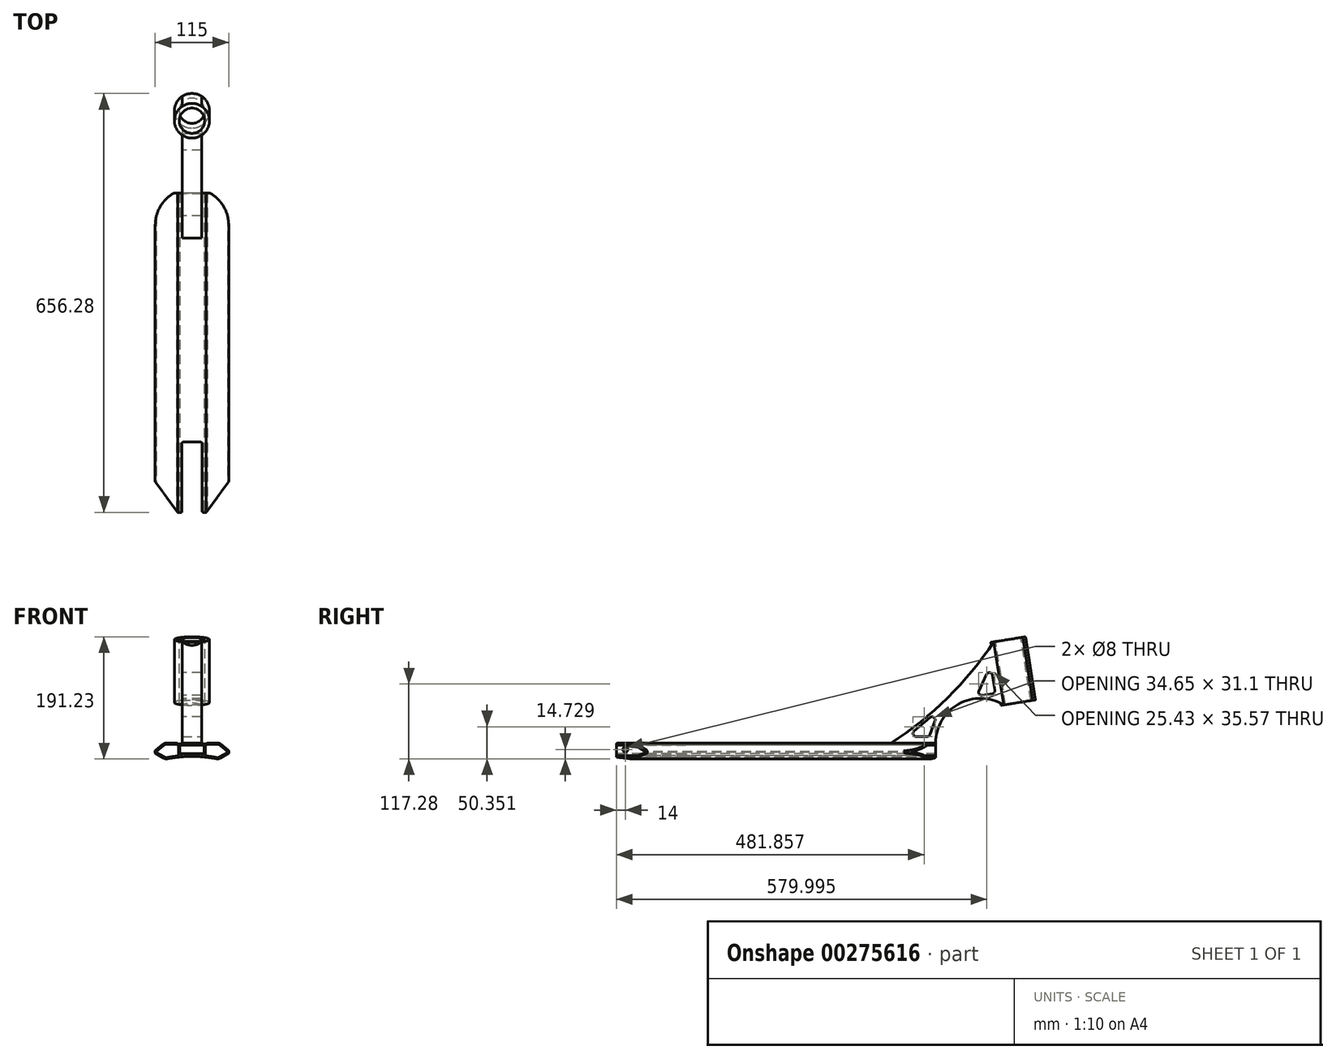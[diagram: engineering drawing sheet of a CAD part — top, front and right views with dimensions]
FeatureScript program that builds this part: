
annotation { "Feature Type Name" : "Feature", "Feature Type Description" : "" }
export const myFeature = defineFeature(function(context is Context, id is Id, definition is map)
    precondition{}
    {
        {
            var Q0;
            Q0=qCreatedBy(makeId("Front.planeOp"),FACE);
            var sketch = newSketch(context, id + "F0", { "sketchPlane" : qUnion([Q0])});
            skLineSegment(sketch, "E0", {"start": v(0, 45.15) * mm, "end": v(0, 0) * mm, "construction": true});
            skLineSegment(sketch, "E1", {"start": v(0, 10.68) * mm, "end": v(22.5, 10.68) * mm});
            skLineSegment(sketch, "E2", {"start": v(22.5, 10.68) * mm, "end": v(22.5, 11.98) * mm});
            skLineSegment(sketch, "E3", {"start": v(22.5, 11.98) * mm, "end": v(43.22, 11.98) * mm});
            skLineSegment(sketch, "E4", {"start": v(43.22, 11.98) * mm, "end": v(57.5, 0) * mm});
            skLineSegment(sketch, "E5", {"start": v(57.5, 0) * mm, "end": v(57.5, -4) * mm});
            skLineSegment(sketch, "E6", {"start": v(57.5, -4) * mm, "end": v(41.36, -13.32) * mm});
            skLineSegment(sketch, "E7.MirrorCS", {"start": v(0, 10.68) * mm, "end": v(-22.5, 10.68) * mm});
            skLineSegment(sketch, "E8.MirrorCS", {"start": v(-22.5, 10.68) * mm, "end": v(-22.5, 11.98) * mm});
            skLineSegment(sketch, "E9.MirrorCS", {"start": v(-22.5, 11.98) * mm, "end": v(-43.22, 11.98) * mm});
            skLineSegment(sketch, "E10.MirrorCS", {"start": v(-43.22, 11.98) * mm, "end": v(-57.5, 0) * mm});
            skLineSegment(sketch, "E11.MirrorCS", {"start": v(-57.5, 0) * mm, "end": v(-57.5, -4) * mm});
            skLineSegment(sketch, "E12.MirrorCS", {"start": v(-57.5, -4) * mm, "end": v(-41.36, -13.32) * mm});
            skArc(sketch, "E13", {"start": v(41.36, -13.32) * mm, "mid": v(0, -9) * mm, "end": v(-41.36, -13.32) * mm});
            skSolve(sketch);
        }
        {
            var Q0;
            Q0=qSketchRegion(id+"F0",true);
            extrude(context, id + "F1", {"entities" : qUnion([Q0]), "endBound" : BoundingType.SYMMETRIC, "depth" : 500 * mm});
        }
        {
            var Q0;
            Q0=makeQuery(id+"F1.opExtrude","CAP_FACE",FACE,{"disambiguationData":[OSD([sQuery(id+"F0.wireOp",EDGE,"E1"),sQuery(id+"F0.wireOp",EDGE,"E2"),sQuery(id+"F0.wireOp",EDGE,"E3"),sQuery(id+"F0.wireOp",EDGE,"E4"),sQuery(id+"F0.wireOp",EDGE,"E5"),sQuery(id+"F0.wireOp",EDGE,"E6"),sQuery(id+"F0.wireOp",EDGE,"E7.MirrorCS"),sQuery(id+"F0.wireOp",EDGE,"E8.MirrorCS"),sQuery(id+"F0.wireOp",EDGE,"E9.MirrorCS"),sQuery(id+"F0.wireOp",EDGE,"E10.MirrorCS"),sQuery(id+"F0.wireOp",EDGE,"E11.MirrorCS"),sQuery(id+"F0.wireOp",EDGE,"E12.MirrorCS"),sQuery(id+"F0.wireOp",EDGE,"E13")])],"isStart":false});
            var sketch = newSketch(context, id + "F2", { "sketchPlane" : qUnion([Q0])});
            skPoint(sketch, "E14.firstSnap0", {"position": v(-50.36, 8.68) * mm});
            skLineSegment(sketch, "E14.top", {"start": v(-19, -4.32) * mm, "end": v(19, -4.32) * mm});
            skLineSegment(sketch, "E14.left", {"start": v(-19, 8.68) * mm, "end": v(-19, -4.32) * mm});
            skLineSegment(sketch, "E14.right", {"start": v(19, 8.68) * mm, "end": v(19, -4.32) * mm});
            skLineSegment(sketch, "E15", {"start": v(-19, 8.68) * mm, "end": v(19, 8.68) * mm});
            skSolve(sketch);
        }
        {
            var Q0;
            Q0=qSketchRegion(id+"F2",true);
            extrude(context, id + "F3", {"entities" : qUnion([Q0]), "operationType" : NewBodyOperationType.REMOVE, "endBound" : BoundingType.THROUGH_ALL, "oppositeDirection" : true, "depth" : 500 * mm});
        }
        {
            var Q0;
            Q0=makeQuery(id+"F1.opExtrude","SWEPT_EDGE",EDGE,{"disambiguationData":[OSD([sQuery(id+"F0.wireOp",EDGE,"E8.MirrorCS"),sQuery(id+"F0.wireOp",EDGE,"E9.MirrorCS")])]});
            var Q1;
            Q1=makeQuery(id+"F1.opExtrude","SWEPT_EDGE",EDGE,{"disambiguationData":[OSD([sQuery(id+"F0.wireOp",EDGE,"E2"),sQuery(id+"F0.wireOp",EDGE,"E3")])]});
            fillet(context, id + "F4", {"entities" : qUnion([Q0, Q1]), "radius" : 2 * mm, "tangentPropagation" : true, "allowEdgeOverflow" : false});
        }
        {
            var Q0;
            Q0=makeQuery(id+"F1.opExtrude","SWEPT_EDGE",EDGE,{"disambiguationData":[OSD([sQuery(id+"F0.wireOp",EDGE,"E12.MirrorCS"),sQuery(id+"F0.wireOp",EDGE,"E13")])]});
            var Q1;
            Q1=makeQuery(id+"F1.opExtrude","SWEPT_EDGE",EDGE,{"disambiguationData":[OSD([sQuery(id+"F0.wireOp",EDGE,"E6"),sQuery(id+"F0.wireOp",EDGE,"E13")])]});
            var Q2;
            Q2=makeQuery(id+"F1.opExtrude","SWEPT_EDGE",EDGE,{"disambiguationData":[OSD([sQuery(id+"F0.wireOp",EDGE,"E9.MirrorCS"),sQuery(id+"F0.wireOp",EDGE,"E10.MirrorCS")])]});
            var Q3;
            Q3=makeQuery(id+"F1.opExtrude","SWEPT_EDGE",EDGE,{"disambiguationData":[OSD([sQuery(id+"F0.wireOp",EDGE,"E3"),sQuery(id+"F0.wireOp",EDGE,"E4")])]});
            fillet(context, id + "F5", {"entities" : qUnion([Q0, Q1, Q2, Q3]), "radius" : 9 * mm, "tangentPropagation" : true, "allowEdgeOverflow" : false});
        }
        {
            var Q0;
            Q0=makeQuery(id+"F1.opExtrude","SWEPT_EDGE",EDGE,{"disambiguationData":[OSD([sQuery(id+"F0.wireOp",EDGE,"E4"),sQuery(id+"F0.wireOp",EDGE,"E5")])]});
            var Q1;
            Q1=makeQuery(id+"F1.opExtrude","SWEPT_EDGE",EDGE,{"disambiguationData":[OSD([sQuery(id+"F0.wireOp",EDGE,"E5"),sQuery(id+"F0.wireOp",EDGE,"E6")])]});
            var Q2;
            Q2=makeQuery(id+"F1.opExtrude","SWEPT_EDGE",EDGE,{"disambiguationData":[OSD([sQuery(id+"F0.wireOp",EDGE,"E10.MirrorCS"),sQuery(id+"F0.wireOp",EDGE,"E11.MirrorCS")])]});
            var Q3;
            Q3=makeQuery(id+"F1.opExtrude","SWEPT_EDGE",EDGE,{"disambiguationData":[OSD([sQuery(id+"F0.wireOp",EDGE,"E11.MirrorCS"),sQuery(id+"F0.wireOp",EDGE,"E12.MirrorCS")])]});
            fillet(context, id + "F6", {"entities" : qUnion([Q0, Q1, Q2, Q3]), "radius" : 1 * mm, "tangentPropagation" : true, "allowEdgeOverflow" : false});
        }
        {
            var Q0;
            Q0=makeQuery(id+"F1.opExtrude","CAP_FACE",FACE,{"disambiguationData":[OSD([sQuery(id+"F0.wireOp",EDGE,"E1"),sQuery(id+"F0.wireOp",EDGE,"E2"),sQuery(id+"F0.wireOp",EDGE,"E3"),sQuery(id+"F0.wireOp",EDGE,"E4"),sQuery(id+"F0.wireOp",EDGE,"E5"),sQuery(id+"F0.wireOp",EDGE,"E6"),sQuery(id+"F0.wireOp",EDGE,"E7.MirrorCS"),sQuery(id+"F0.wireOp",EDGE,"E8.MirrorCS"),sQuery(id+"F0.wireOp",EDGE,"E9.MirrorCS"),sQuery(id+"F0.wireOp",EDGE,"E10.MirrorCS"),sQuery(id+"F0.wireOp",EDGE,"E11.MirrorCS"),sQuery(id+"F0.wireOp",EDGE,"E12.MirrorCS"),sQuery(id+"F0.wireOp",EDGE,"E13")])],"isStart":false});
            var sketch = newSketch(context, id + "F7", { "sketchPlane" : qUnion([Q0])});
            skLineSegment(sketch, "E16.0", {"start": v(-22.5, 10.68) * mm, "end": v(-21, 10.68) * mm});
            skPoint(sketch, "E17.0", {"position": v(-23.23, 11.62) * mm});
            skLineSegment(sketch, "E18.0", {"start": v(-24.37, 11.98) * mm, "end": v(-39.95, 11.98) * mm});
            skArc(sketch, "E19.0", {"start": v(-39.95, 11.98) * mm, "mid": v(-43.02, 11.44) * mm, "end": v(-45.73, 9.88) * mm});
            skLineSegment(sketch, "E20.0", {"start": v(-45.73, 9.88) * mm, "end": v(-57.14, 0.3) * mm});
            skPoint(sketch, "E21.0", {"position": v(-57.4, -0.04) * mm});
            skPoint(sketch, "E22.0", {"position": v(-57.5, -1.94) * mm});
            skPoint(sketch, "E23.0", {"position": v(-57, -4.29) * mm});
            skLineSegment(sketch, "E24.0", {"start": v(-57, -4.29) * mm, "end": v(-44.3, -11.62) * mm});
            skArc(sketch, "E25.0", {"start": v(-44.3, -11.62) * mm, "mid": v(-41.3, -12.7) * mm, "end": v(-38.1, -12.66) * mm});
            skArc(sketch, "E26.0", {"start": v(-21, -10.1) * mm, "mid": v(-29.57, -11.2) * mm, "end": v(-38.1, -12.66) * mm});
            skLineSegment(sketch, "E27", {"start": v(-21, 8.68) * mm, "end": v(-21, -8.1) * mm});
            skLineSegment(sketch, "E28.0", {"start": v(-44.45, 8.34) * mm, "end": v(-55.86, -1.23) * mm});
            skArc(sketch, "E28.1", {"start": v(-39.95, 9.98) * mm, "mid": v(-42.34, 9.56) * mm, "end": v(-44.45, 8.34) * mm});
            skLineSegment(sketch, "E29.0", {"start": v(-24.37, 9.98) * mm, "end": v(-39.95, 9.98) * mm});
            skLineSegment(sketch, "E30.0", {"start": v(-22.5, 8.68) * mm, "end": v(-21, 8.68) * mm});
            skFitSpline(sketch, "E31", {"points": [v(-24.37, 9.98) * mm, v(-22.5, 8.68) * mm], "startDerivative": vector(1.87, -1.3) * mm, "endDerivative": vector(1.87, -1.3) * mm});
            skFitSpline(sketch, "E32", {"points": [v(-23.12, 9.11) * mm, v(-23.48, 9.36) * mm], "startDerivative": vector(-0.35, 0.24) * mm, "endDerivative": vector(-0.35, 0.24) * mm});
            skLineSegment(sketch, "E33.0", {"start": v(-56, -2.56) * mm, "end": v(-43.3, -9.88) * mm});
            skArc(sketch, "E33.1", {"start": v(-43.3, -9.88) * mm, "mid": v(-40.96, -10.73) * mm, "end": v(-38.47, -10.7) * mm});
            skArc(sketch, "E33.2", {"start": v(-21, -8.1) * mm, "mid": v(-29.77, -9.2) * mm, "end": v(-38.47, -10.7) * mm});
            skLineSegment(sketch, "E34", {"start": v(-55.86, -1.23) * mm, "end": v(-56, -2.56) * mm});
            skLineSegment(sketch, "E35.MirrorCS", {"start": v(21, 8.68) * mm, "end": v(21, -8.1) * mm});
            skArc(sketch, "E36.MirrorCS", {"start": v(21, -8.1) * mm, "mid": v(29.77, -9.2) * mm, "end": v(38.47, -10.7) * mm});
            skArc(sketch, "E37.MirrorCS", {"start": v(43.3, -9.88) * mm, "mid": v(40.96, -10.73) * mm, "end": v(38.47, -10.7) * mm});
            skLineSegment(sketch, "E38.MirrorCS", {"start": v(56, -2.56) * mm, "end": v(43.3, -9.88) * mm});
            skLineSegment(sketch, "E39.MirrorCS", {"start": v(55.86, -1.23) * mm, "end": v(56, -2.56) * mm});
            skLineSegment(sketch, "E40.MirrorCS", {"start": v(44.45, 8.34) * mm, "end": v(55.86, -1.23) * mm});
            skArc(sketch, "E41.MirrorCS", {"start": v(39.95, 9.98) * mm, "mid": v(42.34, 9.56) * mm, "end": v(44.45, 8.34) * mm});
            skLineSegment(sketch, "E42.MirrorCS", {"start": v(24.37, 9.98) * mm, "end": v(39.95, 9.98) * mm});
            skLineSegment(sketch, "E43.MirrorCS", {"start": v(22.5, 8.68) * mm, "end": v(21, 8.68) * mm});
            skLineSegment(sketch, "E44", {"start": v(24.37, 9.98) * mm, "end": v(22.5, 8.68) * mm});
            skSolve(sketch);
        }
        {
            var Q0;
            Q0=qSketchRegion(id+"F7",true);
            extrude(context, id + "F8", {"entities" : qUnion([Q0]), "operationType" : NewBodyOperationType.REMOVE, "endBound" : BoundingType.THROUGH_ALL, "oppositeDirection" : true, "depth" : 25 * mm});
        }
        {
            var Q0;
            Q0=qSketchRegion(id+"F7",true);
            extrude(context, id + "F9", {"entities" : qUnion([Q0]), "operationType" : NewBodyOperationType.REMOVE, "endBound" : BoundingType.THROUGH_ALL, "oppositeDirection" : true, "depth" : 25 * mm});
        }
        {
            var Q0;
            Q0=makeQuery(id+"F1.opExtrude","SWEPT_FACE",FACE,{"disambiguationData":[OSD([sQuery(id+"F0.wireOp",EDGE,"E1"),sQuery(id+"F0.wireOp",EDGE,"E7.MirrorCS")])]});
            var sketch = newSketch(context, id + "F10", { "sketchPlane" : qUnion([Q0])});
            skArc(sketch, "E45", {"start": v(57.5, 200) * mm, "mid": v(0, 257.5) * mm, "end": v(-57.5, 200) * mm});
            skLineSegment(sketch, "E46", {"start": v(-57.5, 280) * mm, "end": v(57.5, 280) * mm});
            skLineSegment(sketch, "E47", {"start": v(57.5, 200) * mm, "end": v(57.5, 280) * mm});
            skPoint(sketch, "E48.orphan", {"position": v(63.8, 280) * mm});
            skLineSegment(sketch, "E49", {"start": v(-57.5, 200) * mm, "end": v(-57.5, 280) * mm});
            skPoint(sketch, "E50.orphan", {"position": v(-57.5, 278.01) * mm});
            skSolve(sketch);
        }
        {
            var Q0;
            Q0=qSketchRegion(id+"F10",true);
            extrude(context, id + "F11", {"entities" : qUnion([Q0]), "operationType" : NewBodyOperationType.REMOVE, "endBound" : BoundingType.SYMMETRIC, "oppositeDirection" : true, "depth" : 100 * mm});
        }
        {
            var Q0;
            Q0=makeQuery(id+"F1.opExtrude","SWEPT_FACE",FACE,{"disambiguationData":[OSD([sQuery(id+"F0.wireOp",EDGE,"E9.MirrorCS")])]});
            var sketch = newSketch(context, id + "F12", { "sketchPlane" : qUnion([Q0])});
            skLineSegment(sketch, "E51", {"start": v(-68, -187.37) * mm, "end": v(-22.5, -250) * mm});
            skLineSegment(sketch, "E52", {"start": v(-22.5, -250) * mm, "end": v(-16, -250) * mm});
            skLineSegment(sketch, "E53", {"start": v(-16, -250) * mm, "end": v(-16, -140) * mm});
            skLineSegment(sketch, "E54", {"start": v(-16, -140) * mm, "end": v(16, -140) * mm});
            skLineSegment(sketch, "E55", {"start": v(16, -140) * mm, "end": v(16, -250) * mm});
            skLineSegment(sketch, "E56", {"start": v(16, -250) * mm, "end": v(22.5, -250) * mm});
            skLineSegment(sketch, "E57", {"start": v(22.5, -250) * mm, "end": v(68, -187.37) * mm});
            skLineSegment(sketch, "E58", {"start": v(68, -187.37) * mm, "end": v(68, -287.37) * mm});
            skLineSegment(sketch, "E59", {"start": v(68, -287.37) * mm, "end": v(-68, -287.37) * mm});
            skLineSegment(sketch, "E60", {"start": v(-68, -287.37) * mm, "end": v(-68, -187.37) * mm});
            skSolve(sketch);
        }
        {
            var Q0;
            Q0=qSketchRegion(id+"F12",true);
            extrude(context, id + "F13", {"entities" : qUnion([Q0]), "operationType" : NewBodyOperationType.REMOVE, "endBound" : BoundingType.THROUGH_ALL, "oppositeDirection" : true, "depth" : 25 * mm});
        }
        {
            var Q0;
            {var subQ2=sQuery(id+"F12.wireOp",EDGE,"E53");Q0=makeQuery(id+"F13.boolean.opBoolean","COPY",EDGE,{"disambiguationData":[TD([makeQuery(id+"F3.boolean.opBoolean","COPY",FACE,{"derivedFrom":makeQuery(id+"F3.opExtrude","SWEPT_FACE",FACE,{"disambiguationData":[OSD([sQuery(id+"F2.wireOp",EDGE,"E15")])]})})])],"derivedFrom":makeQuery(id+"F13.opExtrude","SWEPT_EDGE",EDGE,{"disambiguationData":[OSD([sQuery(id+"F12.wireOp",EDGE,"E52"),subQ2])]})});}
            var Q1;
            {var subQ0=sQuery(id+"F0.wireOp",EDGE,"E13");var subQ1=sQuery(id+"F12.wireOp",EDGE,"E53");Q1=makeQuery(id+"F13.boolean.opBoolean","COPY",EDGE,{"disambiguationData":[TD([makeQuery(id+"F1.opExtrude","SWEPT_FACE",FACE,{"disambiguationData":[OSD([subQ0])]})])],"derivedFrom":makeQuery(id+"F13.opExtrude","SWEPT_EDGE",EDGE,{"disambiguationData":[OSD([sQuery(id+"F12.wireOp",EDGE,"E52"),subQ1])]})});}
            var Q2;
            {var subQ0=sQuery(id+"F12.wireOp",EDGE,"E54");var subQ1=sQuery(id+"F12.wireOp",EDGE,"E53");Q2=makeQuery(id+"F13.boolean.opBoolean","COPY",EDGE,{"disambiguationData":[TD([makeQuery(id+"F1.opExtrude","SWEPT_FACE",FACE,{"disambiguationData":[OSD([sQuery(id+"F0.wireOp",EDGE,"E13")])]})])],"derivedFrom":makeQuery(id+"F13.opExtrude","SWEPT_EDGE",EDGE,{"disambiguationData":[OSD([subQ1,subQ0])]})});}
            var Q3;
            {var subQ0=sQuery(id+"F12.wireOp",EDGE,"E53");var subQ1=sQuery(id+"F12.wireOp",EDGE,"E54");Q3=makeQuery(id+"F13.boolean.opBoolean","COPY",EDGE,{"disambiguationData":[TD([makeQuery(id+"F3.boolean.opBoolean","COPY",FACE,{"derivedFrom":makeQuery(id+"F3.opExtrude","SWEPT_FACE",FACE,{"disambiguationData":[OSD([sQuery(id+"F2.wireOp",EDGE,"E15")])]})})])],"derivedFrom":makeQuery(id+"F13.opExtrude","SWEPT_EDGE",EDGE,{"disambiguationData":[OSD([subQ0,subQ1])]})});}
            var Q4;
            {var subQ0=sQuery(id+"F0.wireOp",EDGE,"E13");var subQ1=sQuery(id+"F12.wireOp",EDGE,"E55");Q4=makeQuery(id+"F13.boolean.opBoolean","COPY",EDGE,{"disambiguationData":[TD([makeQuery(id+"F1.opExtrude","SWEPT_FACE",FACE,{"disambiguationData":[OSD([subQ0])]})])],"derivedFrom":makeQuery(id+"F13.opExtrude","SWEPT_EDGE",EDGE,{"disambiguationData":[OSD([subQ1,sQuery(id+"F12.wireOp",EDGE,"E56")])]})});}
            var Q5;
            {var subQ2=sQuery(id+"F12.wireOp",EDGE,"E55");Q5=makeQuery(id+"F13.boolean.opBoolean","COPY",EDGE,{"disambiguationData":[TD([makeQuery(id+"F3.boolean.opBoolean","COPY",FACE,{"derivedFrom":makeQuery(id+"F3.opExtrude","SWEPT_FACE",FACE,{"disambiguationData":[OSD([sQuery(id+"F2.wireOp",EDGE,"E15")])]})})])],"derivedFrom":makeQuery(id+"F13.opExtrude","SWEPT_EDGE",EDGE,{"disambiguationData":[OSD([subQ2,sQuery(id+"F12.wireOp",EDGE,"E56")])]})});}
            var Q6;
            {var subQ0=sQuery(id+"F12.wireOp",EDGE,"E54");var subQ1=sQuery(id+"F12.wireOp",EDGE,"E55");Q6=makeQuery(id+"F13.boolean.opBoolean","COPY",EDGE,{"disambiguationData":[TD([makeQuery(id+"F1.opExtrude","SWEPT_FACE",FACE,{"disambiguationData":[OSD([sQuery(id+"F0.wireOp",EDGE,"E13")])]})])],"derivedFrom":makeQuery(id+"F13.opExtrude","SWEPT_EDGE",EDGE,{"disambiguationData":[OSD([subQ0,subQ1])]})});}
            var Q7;
            {var subQ0=sQuery(id+"F12.wireOp",EDGE,"E54");var subQ1=sQuery(id+"F12.wireOp",EDGE,"E55");Q7=makeQuery(id+"F13.boolean.opBoolean","COPY",EDGE,{"disambiguationData":[TD([makeQuery(id+"F3.boolean.opBoolean","COPY",FACE,{"derivedFrom":makeQuery(id+"F3.opExtrude","SWEPT_FACE",FACE,{"disambiguationData":[OSD([sQuery(id+"F2.wireOp",EDGE,"E15")])]})})])],"derivedFrom":makeQuery(id+"F13.opExtrude","SWEPT_EDGE",EDGE,{"disambiguationData":[OSD([subQ0,subQ1])]})});}
            fillet(context, id + "F14", {"entities" : qUnion([Q0, Q1, Q2, Q3, Q4, Q5, Q6, Q7]), "radius" : 2 * mm, "tangentPropagation" : true, "allowEdgeOverflow" : false});
        }
        {
            var Q0;
            Q0=qCreatedBy(makeId("Right.planeOp"),FACE);
            var sketch = newSketch(context, id + "F15", { "sketchPlane" : qUnion([Q0])});
            skLineSegment(sketch, "E61", {"start": v(180, 11.98) * mm, "end": v(250, 11.98) * mm});
            skArc(sketch, "E62", {"start": v(356.44, 71.75) * mm, "mid": v(285.73, 73.02) * mm, "end": v(250, 11.98) * mm});
            skLineSegment(sketch, "E63", {"start": v(356.44, 71.75) * mm, "end": v(401.87, 78.94) * mm});
            skLineSegment(sketch, "E64", {"start": v(401.87, 78.94) * mm, "end": v(386.23, 177.71) * mm});
            skLineSegment(sketch, "E65", {"start": v(386.23, 177.71) * mm, "end": v(340.8, 170.52) * mm});
            skArc(sketch, "E66", {"start": v(180, 11.98) * mm, "mid": v(268.62, 82.9) * mm, "end": v(340.8, 170.52) * mm});
            skSolve(sketch);
        }
        {
            var Q0;
            Q0=qSketchRegion(id+"F15",true);
            extrude(context, id + "F16", {"entities" : qUnion([Q0]), "operationType" : NewBodyOperationType.ADD, "endBound" : BoundingType.SYMMETRIC, "depth" : 30 * mm});
        }
        {
            var Q0;
            Q0=makeQuery(id+"F16.opExtrude","SWEPT_FACE",FACE,{"disambiguationData":[OSD([sQuery(id+"F15.wireOp",EDGE,"E65")])]});
            var sketch = newSketch(context, id + "F17", { "sketchPlane" : qUnion([Q0])});
            skCircle(sketch, "E67", {"center": v(0, 386.28) * mm, "radius": 27.46 * mm});
            skSolve(sketch);
        }
        {
            var Q0;
            Q0=qSketchRegion(id+"F17",true);
            var Q1;
            Q1=makeQuery(id+"F16.opExtrude","SWEPT_FACE",FACE,{"disambiguationData":[OSD([sQuery(id+"F15.wireOp",EDGE,"E63")])]});
            var Q2;
            Q2=makeQuery(id+"F16.opExtrude","SWEPT_BODY",BODY,{"disambiguationData":[OSD([sQuery(id+"F15.wireOp",EDGE,"E61"),sQuery(id+"F15.wireOp",EDGE,"E62"),sQuery(id+"F15.wireOp",EDGE,"E63"),sQuery(id+"F15.wireOp",EDGE,"E64"),sQuery(id+"F15.wireOp",EDGE,"E65"),sQuery(id+"F15.wireOp",EDGE,"E66")])]});
            extrude(context, id + "F18", {"entities" : qUnion([Q0]), "operationType" : NewBodyOperationType.ADD, "endBound" : BoundingType.UP_TO_SURFACE, "oppositeDirection" : true, "endBoundEntityFace" : qUnion([Q1]), "endBoundEntityBody" : qUnion([Q2]), "depth" : 25 * mm});
        }
        {
            var Q0;
            Q0=makeQuery(id+"F18.boolean.opBoolean","MERGE",FACE,{"derivedFrom":[makeQuery(id+"F16.opExtrude","SWEPT_FACE",FACE,{"disambiguationData":[OSD([sQuery(id+"F15.wireOp",EDGE,"E65")])]}),makeQuery(id+"F18.opExtrude","CAP_FACE",FACE,{"disambiguationData":[OSD([sQuery(id+"F17.wireOp",EDGE,"E67")])],"isStart":true})]});
            var sketch = newSketch(context, id + "F19", { "sketchPlane" : qUnion([Q0])});
            skPoint(sketch, "E68", {"position": v(0, 386.28) * mm});
            skSolve(sketch);
        }
        {
            var Q0;
            Q0=sQuery(id+"F19.wireOp",VERTEX,"E68");
            var Q1;
            Q1=makeQuery(id+"F16.opExtrude","SWEPT_BODY",BODY,{"disambiguationData":[OSD([sQuery(id+"F15.wireOp",EDGE,"E61"),sQuery(id+"F15.wireOp",EDGE,"E62"),sQuery(id+"F15.wireOp",EDGE,"E63"),sQuery(id+"F15.wireOp",EDGE,"E64"),sQuery(id+"F15.wireOp",EDGE,"E65"),sQuery(id+"F15.wireOp",EDGE,"E66")])]});
            hole(context, id + "F20", {"style" : HoleStyle.SIMPLE, "endStyle" : HoleEndStyle.THROUGH, "holeDiameter" : 40 * mm, "locations" : qUnion([Q0]), "scope" : qUnion([Q1]), "isTappedThrough" : true});
        }
        {
            var Q0;
            Q0=makeQuery(id+"F8.boolean.opBoolean","COPY",FACE,{"derivedFrom":makeQuery(id+"F8.opExtrude","SWEPT_FACE",FACE,{"disambiguationData":[OSD([sQuery(id+"F7.wireOp",EDGE,"E35.MirrorCS")])]})});
            var sketch = newSketch(context, id + "F21", { "sketchPlane" : qUnion([Q0])});
            skPoint(sketch, "E69", {"position": v(-236, 1.9) * mm});
            skSolve(sketch);
        }
        {
            var Q0;
            Q0=sQuery(id+"F21.wireOp",VERTEX,"E69");
            var Q1;
            Q1=makeQuery(id+"F1.opExtrude","SWEPT_BODY",BODY,{"disambiguationData":[OSD([sQuery(id+"F0.wireOp",EDGE,"E1"),sQuery(id+"F0.wireOp",EDGE,"E2"),sQuery(id+"F0.wireOp",EDGE,"E3"),sQuery(id+"F0.wireOp",EDGE,"E4"),sQuery(id+"F0.wireOp",EDGE,"E5"),sQuery(id+"F0.wireOp",EDGE,"E6"),sQuery(id+"F0.wireOp",EDGE,"E7.MirrorCS"),sQuery(id+"F0.wireOp",EDGE,"E8.MirrorCS"),sQuery(id+"F0.wireOp",EDGE,"E9.MirrorCS"),sQuery(id+"F0.wireOp",EDGE,"E10.MirrorCS"),sQuery(id+"F0.wireOp",EDGE,"E11.MirrorCS"),sQuery(id+"F0.wireOp",EDGE,"E12.MirrorCS"),sQuery(id+"F0.wireOp",EDGE,"E13")])]});
            hole(context, id + "F22", {"style" : HoleStyle.SIMPLE, "endStyle" : HoleEndStyle.THROUGH, "holeDiameter" : 8 * mm, "locations" : qUnion([Q0]), "scope" : qUnion([Q1]), "isTappedThrough" : true});
        }
        {
            var Q0;
            Q0=makeQuery(id+"F1.opExtrude","SWEPT_FACE",FACE,{"disambiguationData":[OSD([sQuery(id+"F0.wireOp",EDGE,"E5")])]});
            var sketch = newSketch(context, id + "F23", { "sketchPlane" : qUnion([Q0])});
            skLineSegment(sketch, "E70", {"start": v(206, 21.98) * mm, "end": v(240, 21.98) * mm});
            skLineSegment(sketch, "E71", {"start": v(240, 21.98) * mm, "end": v(255.4, 64.27) * mm});
            skLineSegment(sketch, "E72", {"start": v(255.4, 64.27) * mm, "end": v(206, 21.98) * mm});
            skLineSegment(sketch, "E73", {"start": v(336.4, 134.38) * mm, "end": v(313.8, 85.24) * mm});
            skLineSegment(sketch, "E74", {"start": v(313.8, 85.24) * mm, "end": v(343.43, 89.94) * mm});
            skLineSegment(sketch, "E75", {"start": v(343.43, 89.94) * mm, "end": v(336.4, 134.38) * mm});
            skSolve(sketch);
        }
        {
            var Q0;
            Q0=qSketchRegion(id+"F23",true);
            extrude(context, id + "F24", {"entities" : qUnion([Q0]), "operationType" : NewBodyOperationType.REMOVE, "endBound" : BoundingType.THROUGH_ALL, "oppositeDirection" : true, "depth" : 25 * mm});
        }
        {
            var Q0;
            Q0=makeQuery(id+"F24.boolean.opBoolean","COPY",EDGE,{"derivedFrom":makeQuery(id+"F24.opExtrude","SWEPT_EDGE",EDGE,{"disambiguationData":[OSD([sQuery(id+"F23.wireOp",EDGE,"E74"),sQuery(id+"F23.wireOp",EDGE,"E75")])]})});
            var Q1;
            Q1=makeQuery(id+"F24.boolean.opBoolean","COPY",EDGE,{"derivedFrom":makeQuery(id+"F24.opExtrude","SWEPT_EDGE",EDGE,{"disambiguationData":[OSD([sQuery(id+"F23.wireOp",EDGE,"E70"),sQuery(id+"F23.wireOp",EDGE,"E71")])]})});
            var Q2;
            Q2=makeQuery(id+"F24.boolean.opBoolean","COPY",EDGE,{"derivedFrom":makeQuery(id+"F24.opExtrude","SWEPT_EDGE",EDGE,{"disambiguationData":[OSD([sQuery(id+"F23.wireOp",EDGE,"E71"),sQuery(id+"F23.wireOp",EDGE,"E72")])]})});
            var Q3;
            Q3=makeQuery(id+"F24.boolean.opBoolean","COPY",EDGE,{"derivedFrom":makeQuery(id+"F24.opExtrude","SWEPT_EDGE",EDGE,{"disambiguationData":[OSD([sQuery(id+"F23.wireOp",EDGE,"E73"),sQuery(id+"F23.wireOp",EDGE,"E75")])]})});
            var Q4;
            Q4=makeQuery(id+"F24.boolean.opBoolean","COPY",EDGE,{"derivedFrom":makeQuery(id+"F24.opExtrude","SWEPT_EDGE",EDGE,{"disambiguationData":[OSD([sQuery(id+"F23.wireOp",EDGE,"E73"),sQuery(id+"F23.wireOp",EDGE,"E74")])]})});
            var Q5;
            Q5=makeQuery(id+"F24.boolean.opBoolean","COPY",EDGE,{"derivedFrom":makeQuery(id+"F24.opExtrude","SWEPT_EDGE",EDGE,{"disambiguationData":[OSD([sQuery(id+"F23.wireOp",EDGE,"E70"),sQuery(id+"F23.wireOp",EDGE,"E72")])]})});
            fillet(context, id + "F25", {"entities" : qUnion([Q0, Q1, Q2, Q3, Q4, Q5]), "radius" : 5 * mm, "tangentPropagation" : true, "allowEdgeOverflow" : false});
        }
    });
